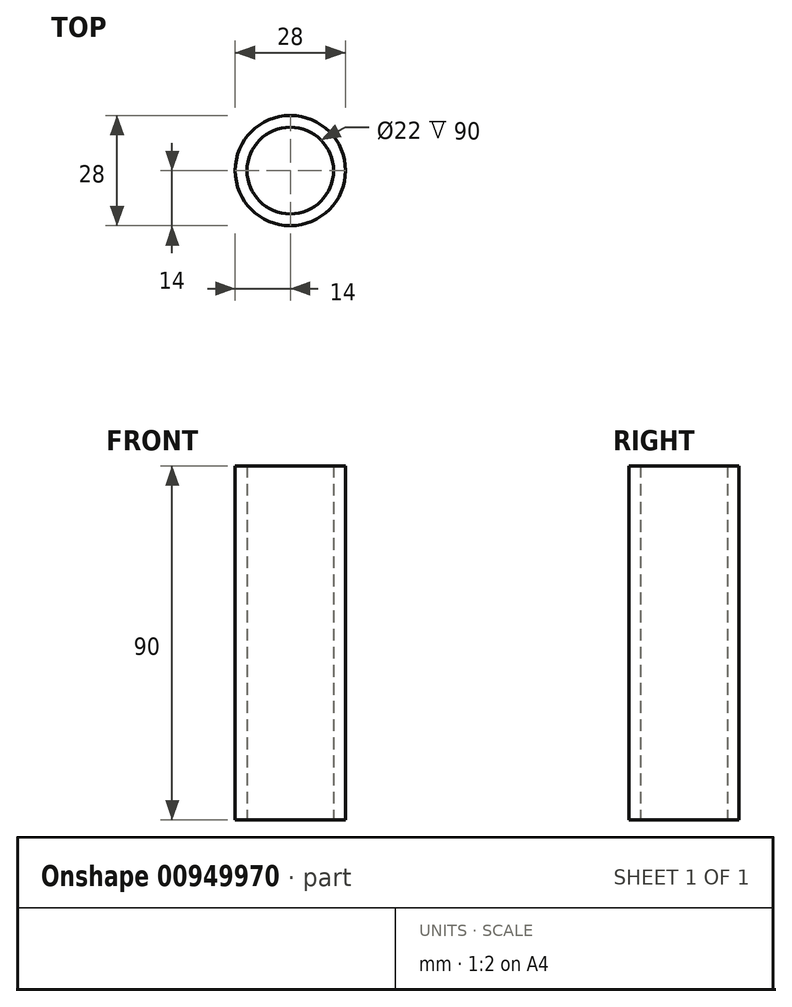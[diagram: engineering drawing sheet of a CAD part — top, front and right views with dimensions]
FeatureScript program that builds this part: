
annotation { "Feature Type Name" : "Feature", "Feature Type Description" : "" }
export const myFeature = defineFeature(function(context is Context, id is Id, definition is map)
    precondition{}
    {
        {
            var Q0;
            Q0=qCreatedBy(makeId("Top.planeOp"),FACE);
            var sketch = newSketch(context, id + "F0", { "sketchPlane" : qUnion([Q0])});
            skCircle(sketch, "E0", {"center": v(0, 0) * mm, "radius": 14 * mm});
            skCircle(sketch, "E1", {"center": v(0, 0) * mm, "radius": 11 * mm});
            skSolve(sketch);
        }
        {
            var Q0;
            Q0 = qSketchRegion(id + "F0", true);
            extrude(context, id + "F1", {"entities" : qUnion([Q0]), "depth" : 90 * mm, "offsetDistance" : 25 * mm});
        }
    });
